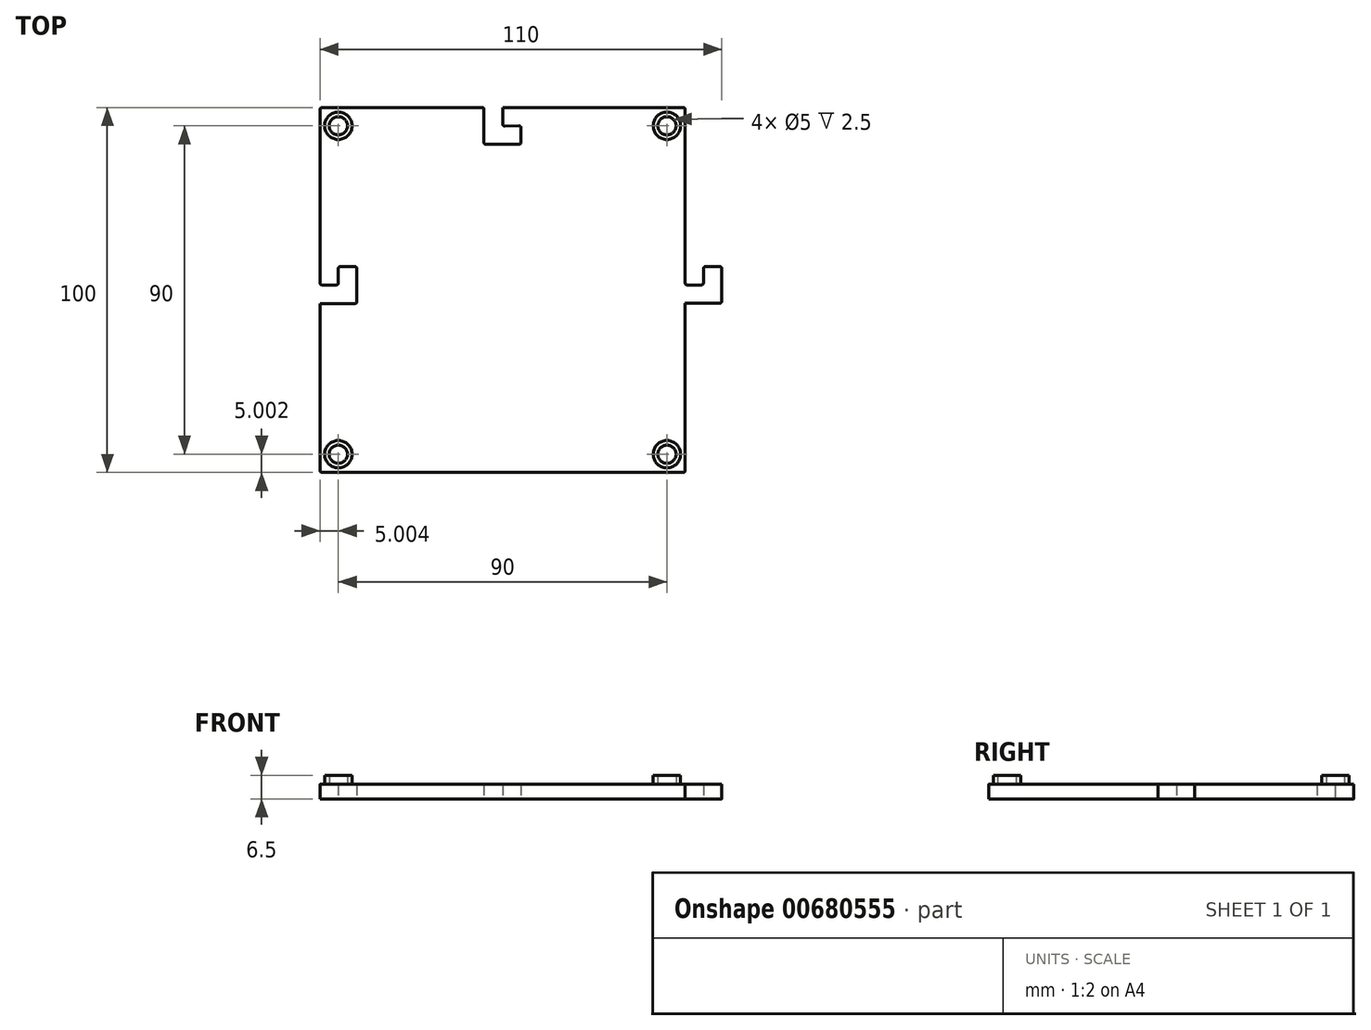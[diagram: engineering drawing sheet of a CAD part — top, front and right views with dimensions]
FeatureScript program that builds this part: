
annotation { "Feature Type Name" : "Feature", "Feature Type Description" : "" }
export const myFeature = defineFeature(function(context is Context, id is Id, definition is map)
    precondition{}
    {
        {
            var Q0;
            Q0=qCreatedBy(makeId("Top.planeOp"),FACE);
            var sketch = newSketch(context, id + "F0", { "sketchPlane" : qUnion([Q0])});
            skLineSegment(sketch, "E0.bottom", {"start": v(-68.75, 48.6) * mm, "end": v(31.25, 48.6) * mm});
            skLineSegment(sketch, "E0.top", {"start": v(-68.75, -51.4) * mm, "end": v(31.25, -51.4) * mm});
            skLineSegment(sketch, "E0.left", {"start": v(-68.75, 48.6) * mm, "end": v(-68.75, -51.4) * mm});
            skLineSegment(sketch, "E0.right", {"start": v(31.25, 48.6) * mm, "end": v(31.25, -51.4) * mm});
            skSolve(sketch);
        }
        {
            var Q0;
            Q0=makeQuery(id+"F0.imprint","IMPRINT",FACE,{"disambiguationData":[TD([[makeQuery(id+"F0.imprint","IMPRINT",EDGE,{"derivedFrom":sQuery(id+"F0.wireOp",EDGE,"E0.bottom")}),-1.0]])]});
            extrude(context, id + "F1", {"entities" : qUnion([Q0]), "depth" : 4 * mm, "offsetDistance" : 25 * mm});
        }
        {
            var Q0;
            Q0=makeQuery(id+"F1.opExtrude","CAP_FACE",FACE,{"disambiguationData":[OSD([sQuery(id+"F0.wireOp",EDGE,"E0.bottom"),sQuery(id+"F0.wireOp",EDGE,"E0.top"),sQuery(id+"F0.wireOp",EDGE,"E0.left"),sQuery(id+"F0.wireOp",EDGE,"E0.right")])],"isStart":true});
            var sketch = newSketch(context, id + "F2", { "sketchPlane" : qUnion([Q0])});
            skLineSegment(sketch, "E1.bottom", {"start": v(-18.75, 51.4) * mm, "end": v(-23.75, 51.4) * mm});
            skLineSegment(sketch, "E1.top", {"start": v(-18.75, 51.4) * mm, "end": v(-23.75, 51.4) * mm});
            skLineSegment(sketch, "E1.left", {"start": v(-18.75, 51.4) * mm, "end": v(-18.75, 51.4) * mm});
            skLineSegment(sketch, "E1.right", {"start": v(-23.75, 51.4) * mm, "end": v(-23.75, 51.4) * mm});
            skLineSegment(sketch, "E2", {"start": v(-18.75, 51.4) * mm, "end": v(-13.75, 51.4) * mm});
            skLineSegment(sketch, "E3", {"start": v(-23.75, 51.4) * mm, "end": v(-23.75, 61.4) * mm});
            skLineSegment(sketch, "E4", {"start": v(-23.75, 61.4) * mm, "end": v(-13.75, 61.4) * mm});
            skLineSegment(sketch, "E5", {"start": v(-13.75, 61.4) * mm, "end": v(-13.75, 51.4) * mm});
            skLineSegment(sketch, "E6", {"start": v(-18.75, 51.4) * mm, "end": v(-18.75, 56.4) * mm});
            skLineSegment(sketch, "E7", {"start": v(-18.75, 56.4) * mm, "end": v(-13.75, 56.4) * mm});
            skLineSegment(sketch, "E8", {"start": v(31.25, 0) * mm, "end": v(31.25, 5) * mm});
            skLineSegment(sketch, "E9", {"start": v(31.25, 0) * mm, "end": v(31.25, -5) * mm});
            skLineSegment(sketch, "E10", {"start": v(31.25, 5) * mm, "end": v(41.25, 5) * mm});
            skLineSegment(sketch, "E11", {"start": v(41.25, 5) * mm, "end": v(41.25, -5) * mm});
            skLineSegment(sketch, "E12", {"start": v(31.25, -5) * mm, "end": v(41.25, -5) * mm});
            skLineSegment(sketch, "E13", {"start": v(31.25, 0) * mm, "end": v(36.25, 0) * mm});
            skPoint(sketch, "E13.endSnap0", {"position": v(41.25, 0) * mm});
            skLineSegment(sketch, "E14", {"start": v(36.25, 0) * mm, "end": v(36.25, -5) * mm});
            skLineSegment(sketch, "E15", {"start": v(-18.75, -48.6) * mm, "end": v(-23.75, -48.6) * mm});
            skLineSegment(sketch, "E16", {"start": v(-18.75, -48.6) * mm, "end": v(-13.75, -48.6) * mm});
            skLineSegment(sketch, "E17", {"start": v(-23.75, -48.6) * mm, "end": v(-23.75, -38.6) * mm});
            skLineSegment(sketch, "E18", {"start": v(-23.75, -38.6) * mm, "end": v(-13.75, -38.6) * mm});
            skLineSegment(sketch, "E19", {"start": v(-13.75, -38.6) * mm, "end": v(-13.75, -48.6) * mm});
            skLineSegment(sketch, "E20", {"start": v(-18.75, -48.6) * mm, "end": v(-18.75, -43.6) * mm});
            skLineSegment(sketch, "E21", {"start": v(-18.75, -43.6) * mm, "end": v(-13.75, -43.6) * mm});
            skLineSegment(sketch, "E22", {"start": v(-68.75, 0) * mm, "end": v(-68.75, 5) * mm});
            skLineSegment(sketch, "E23", {"start": v(-68.75, 0) * mm, "end": v(-68.75, -5) * mm});
            skLineSegment(sketch, "E24", {"start": v(-68.75, 5) * mm, "end": v(-58.75, 5) * mm});
            skLineSegment(sketch, "E25", {"start": v(-58.75, 5) * mm, "end": v(-58.75, -5) * mm});
            skLineSegment(sketch, "E26", {"start": v(-68.75, -5) * mm, "end": v(-58.75, -5) * mm});
            skLineSegment(sketch, "E27", {"start": v(-68.75, 0) * mm, "end": v(-63.75, 0) * mm});
            skLineSegment(sketch, "E28", {"start": v(-63.75, 0) * mm, "end": v(-63.75, -5) * mm});
            skSolve(sketch);
        }
        {
            var Q0;
            Q0=makeQuery(id+"F2.imprint","IMPRINT",FACE,{"disambiguationData":[TD([[makeQuery(id+"F2.imprint","IMPRINT",EDGE,{"derivedFrom":sQuery(id+"F2.wireOp",EDGE,"E1.top")}),1.0]])]});
            var Q1;
            Q1=makeQuery(id+"F2.imprint","IMPRINT",FACE,{"disambiguationData":[TD([[makeQuery(id+"F2.imprint","IMPRINT",EDGE,{"derivedFrom":sQuery(id+"F2.wireOp",EDGE,"E8")}),-1.0]])]});
            extrude(context, id + "F3", {"entities" : qUnion([Q0, Q1]), "oppositeDirection" : true, "depth" : 4 * mm, "offsetDistance" : 25 * mm});
        }
        {
            var Q0;
            Q0=makeQuery(id+"F1.opExtrude","CAP_FACE",FACE,{"disambiguationData":[OSD([sQuery(id+"F0.wireOp",EDGE,"E0.bottom"),sQuery(id+"F0.wireOp",EDGE,"E0.top"),sQuery(id+"F0.wireOp",EDGE,"E0.left"),sQuery(id+"F0.wireOp",EDGE,"E0.right")])],"isStart":true});
            var sketch = newSketch(context, id + "F4", { "sketchPlane" : qUnion([Q0])});
            skLineSegment(sketch, "E29", {"start": v(-18.75, -48.6) * mm, "end": v(-23.85, -48.6) * mm});
            skLineSegment(sketch, "E30", {"start": v(-23.85, -48.6) * mm, "end": v(-23.85, -38.5) * mm});
            skLineSegment(sketch, "E31", {"start": v(-18.75, -48.6) * mm, "end": v(-18.75, -43.55) * mm});
            skPoint(sketch, "E31.endSnap0", {"position": v(-23.85, -43.55) * mm});
            skLineSegment(sketch, "E32", {"start": v(-18.75, -43.55) * mm, "end": v(-13.75, -43.6) * mm});
            skLineSegment(sketch, "E33", {"start": v(-68.75, 0) * mm, "end": v(-68.75, 5.1) * mm});
            skLineSegment(sketch, "E34", {"start": v(-68.75, 5.1) * mm, "end": v(-58.65, 5.1) * mm});
            skLineSegment(sketch, "E35", {"start": v(-68.75, 0) * mm, "end": v(-63.75, 0) * mm});
            skLineSegment(sketch, "E36", {"start": v(-63.75, 0) * mm, "end": v(-63.75, -5) * mm});
            skLineSegment(sketch, "E37", {"start": v(-63.75, -5) * mm, "end": v(-58.65, -5) * mm});
            skLineSegment(sketch, "E38", {"start": v(-58.65, 5.1) * mm, "end": v(-58.65, -5) * mm});
            skLineSegment(sketch, "E39", {"start": v(-13.75, -43.6) * mm, "end": v(-13.75, -38.5) * mm});
            skLineSegment(sketch, "E40", {"start": v(-23.85, -38.5) * mm, "end": v(-13.75, -38.5) * mm});
            skSolve(sketch);
        }
        {
            var Q0;
            Q0 = qSketchRegion(id + "F4", true);
            extrude(context, id + "F5", {"entities" : qUnion([Q0]), "operationType" : NewBodyOperationType.REMOVE, "oppositeDirection" : true, "depth" : 25 * mm, "offsetDistance" : 25 * mm});
        }
        {
            var Q0;
            Q0=makeQuery(id+"F1.opExtrude","SWEPT_EDGE",EDGE,{"disambiguationData":[OSD([sQuery(id+"F0.wireOp",EDGE,"E0.top"),sQuery(id+"F0.wireOp",EDGE,"E0.right")])]});
            var Q1;
            Q1=makeQuery(id+"F1.opExtrude","SWEPT_EDGE",EDGE,{"disambiguationData":[OSD([sQuery(id+"F0.wireOp",EDGE,"E0.bottom"),sQuery(id+"F0.wireOp",EDGE,"E0.right")])]});
            var Q2;
            Q2=makeQuery(id+"F1.opExtrude","SWEPT_EDGE",EDGE,{"disambiguationData":[OSD([sQuery(id+"F0.wireOp",EDGE,"E0.bottom"),sQuery(id+"F0.wireOp",EDGE,"E0.left")])]});
            var Q3;
            Q3=makeQuery(id+"F1.opExtrude","SWEPT_EDGE",EDGE,{"disambiguationData":[OSD([sQuery(id+"F0.wireOp",EDGE,"E0.top"),sQuery(id+"F0.wireOp",EDGE,"E0.left")])]});
            fillet(context, id + "F6", {"entities" : qUnion([Q0, Q1, Q2, Q3]), "radius" : 0.5 * mm, "tangentPropagation" : true, "allowEdgeOverflow" : false});
        }
        {
            var Q0;
            Q0=makeQuery(id+"F3.opExtrude","SWEPT_BODY",BODY,{"disambiguationData":[OSD([sQuery(id+"F2.wireOp",EDGE,"E1.top"),sQuery(id+"F2.wireOp",EDGE,"E3"),sQuery(id+"F2.wireOp",EDGE,"E4"),sQuery(id+"F2.wireOp",EDGE,"E5"),sQuery(id+"F2.wireOp",EDGE,"E6"),sQuery(id+"F2.wireOp",EDGE,"E7")])]});
            var Q1;
            Q1=makeQuery(id+"F1.opExtrude","SWEPT_BODY",BODY,{"disambiguationData":[OSD([sQuery(id+"F0.wireOp",EDGE,"E0.bottom"),sQuery(id+"F0.wireOp",EDGE,"E0.top"),sQuery(id+"F0.wireOp",EDGE,"E0.left"),sQuery(id+"F0.wireOp",EDGE,"E0.right")])]});
            var Q2;
            Q2=makeQuery(id+"F3.opExtrude","SWEPT_BODY",BODY,{"disambiguationData":[OSD([sQuery(id+"F2.wireOp",EDGE,"E8"),sQuery(id+"F2.wireOp",EDGE,"E10"),sQuery(id+"F2.wireOp",EDGE,"E11"),sQuery(id+"F2.wireOp",EDGE,"E12"),sQuery(id+"F2.wireOp",EDGE,"E13"),sQuery(id+"F2.wireOp",EDGE,"E14")])]});
            booleanBodies(context, id + "F7", {"operationType" : BooleanOperationType.UNION, "tools" : qUnion([Q0, Q1, Q2])});
        }
        {
            var Q0;
            Q0=makeQuery(id+"F3.opExtrude","SWEPT_EDGE",EDGE,{"disambiguationData":[OSD([sQuery(id+"F0.wireOp",EDGE,"E0.top"),sQuery(id+"F2.wireOp",EDGE,"E1.top"),sQuery(id+"F2.wireOp",EDGE,"E3")])]});
            var Q1;
            Q1=makeQuery(id+"F3.opExtrude","SWEPT_EDGE",EDGE,{"disambiguationData":[OSD([sQuery(id+"F2.wireOp",EDGE,"E1.top"),sQuery(id+"F2.wireOp",EDGE,"E2"),sQuery(id+"F2.wireOp",EDGE,"E6")])]});
            var Q2;
            Q2=makeQuery(id+"F3.opExtrude","SWEPT_EDGE",EDGE,{"disambiguationData":[OSD([sQuery(id+"F2.wireOp",EDGE,"E4"),sQuery(id+"F2.wireOp",EDGE,"E5")])]});
            var Q3;
            Q3=makeQuery(id+"F3.opExtrude","SWEPT_EDGE",EDGE,{"disambiguationData":[OSD([sQuery(id+"F2.wireOp",EDGE,"E5"),sQuery(id+"F2.wireOp",EDGE,"E7")])]});
            var Q4;
            Q4=makeQuery(id+"F3.opExtrude","SWEPT_EDGE",EDGE,{"disambiguationData":[OSD([sQuery(id+"F2.wireOp",EDGE,"E6"),sQuery(id+"F2.wireOp",EDGE,"E7")])]});
            var Q5;
            Q5=makeQuery(id+"F3.opExtrude","SWEPT_EDGE",EDGE,{"disambiguationData":[OSD([sQuery(id+"F2.wireOp",EDGE,"E3"),sQuery(id+"F2.wireOp",EDGE,"E4")])]});
            var Q6;
            Q6=makeQuery(id+"F3.opExtrude","SWEPT_EDGE",EDGE,{"disambiguationData":[OSD([sQuery(id+"F0.wireOp",EDGE,"E0.right"),sQuery(id+"F2.wireOp",EDGE,"E8"),sQuery(id+"F2.wireOp",EDGE,"E10")])]});
            var Q7;
            Q7=makeQuery(id+"F3.opExtrude","SWEPT_EDGE",EDGE,{"disambiguationData":[OSD([sQuery(id+"F2.wireOp",EDGE,"E10"),sQuery(id+"F2.wireOp",EDGE,"E11")])]});
            var Q8;
            Q8=makeQuery(id+"F3.opExtrude","SWEPT_EDGE",EDGE,{"disambiguationData":[OSD([sQuery(id+"F2.wireOp",EDGE,"E11"),sQuery(id+"F2.wireOp",EDGE,"E12")])]});
            var Q9;
            Q9=makeQuery(id+"F3.opExtrude","SWEPT_EDGE",EDGE,{"disambiguationData":[OSD([sQuery(id+"F2.wireOp",EDGE,"E12"),sQuery(id+"F2.wireOp",EDGE,"E14")])]});
            var Q10;
            Q10=makeQuery(id+"F3.opExtrude","SWEPT_EDGE",EDGE,{"disambiguationData":[OSD([sQuery(id+"F2.wireOp",EDGE,"E13"),sQuery(id+"F2.wireOp",EDGE,"E14")])]});
            var Q11;
            Q11=makeQuery(id+"F3.opExtrude","SWEPT_EDGE",EDGE,{"disambiguationData":[OSD([sQuery(id+"F2.wireOp",EDGE,"E8"),sQuery(id+"F2.wireOp",EDGE,"E9"),sQuery(id+"F2.wireOp",EDGE,"E13")])]});
            var Q12;
            Q12=makeQuery(id+"F5.boolean.opBoolean","COPY",EDGE,{"derivedFrom":makeQuery(id+"F5.opExtrude","SWEPT_EDGE",EDGE,{"disambiguationData":[OSD([sQuery(id+"F4.wireOp",EDGE,"E30"),sQuery(id+"F4.wireOp",EDGE,"E40")])]})});
            var Q13;
            Q13=makeQuery(id+"F5.boolean.opBoolean","COPY",EDGE,{"derivedFrom":makeQuery(id+"F5.opExtrude","SWEPT_EDGE",EDGE,{"disambiguationData":[OSD([sQuery(id+"F4.wireOp",EDGE,"E39"),sQuery(id+"F4.wireOp",EDGE,"E40")])]})});
            var Q14;
            Q14=makeQuery(id+"F5.boolean.opBoolean","COPY",EDGE,{"derivedFrom":makeQuery(id+"F5.opExtrude","SWEPT_EDGE",EDGE,{"disambiguationData":[OSD([sQuery(id+"F0.wireOp",EDGE,"E0.bottom"),sQuery(id+"F4.wireOp",EDGE,"E29"),sQuery(id+"F4.wireOp",EDGE,"E31")])]})});
            var Q15;
            Q15=makeQuery(id+"F5.boolean.opBoolean","COPY",EDGE,{"derivedFrom":makeQuery(id+"F5.opExtrude","SWEPT_EDGE",EDGE,{"disambiguationData":[OSD([sQuery(id+"F4.wireOp",EDGE,"E31"),sQuery(id+"F4.wireOp",EDGE,"E32")])]})});
            var Q16;
            Q16=makeQuery(id+"F5.boolean.opBoolean","COPY",EDGE,{"derivedFrom":makeQuery(id+"F5.opExtrude","SWEPT_EDGE",EDGE,{"disambiguationData":[OSD([sQuery(id+"F0.wireOp",EDGE,"E0.bottom"),sQuery(id+"F4.wireOp",EDGE,"E29"),sQuery(id+"F4.wireOp",EDGE,"E30")])]})});
            var Q17;
            Q17=makeQuery(id+"F5.boolean.opBoolean","COPY",EDGE,{"derivedFrom":makeQuery(id+"F5.opExtrude","SWEPT_EDGE",EDGE,{"disambiguationData":[OSD([sQuery(id+"F4.wireOp",EDGE,"E32"),sQuery(id+"F4.wireOp",EDGE,"E39")])]})});
            fillet(context, id + "F8", {"entities" : qUnion([Q0, Q1, Q2, Q3, Q4, Q5, Q6, Q7, Q8, Q9, Q10, Q11, Q12, Q13, Q14, Q15, Q16, Q17]), "radius" : 0.5 * mm, "tangentPropagation" : true, "allowEdgeOverflow" : false});
        }
        {
            var Q0;
            Q0=makeQuery(id+"F5.boolean.opBoolean","COPY",EDGE,{"derivedFrom":makeQuery(id+"F5.opExtrude","SWEPT_EDGE",EDGE,{"disambiguationData":[OSD([sQuery(id+"F4.wireOp",EDGE,"E37"),sQuery(id+"F4.wireOp",EDGE,"E38")])]})});
            var Q1;
            Q1=makeQuery(id+"F5.boolean.opBoolean","COPY",EDGE,{"derivedFrom":makeQuery(id+"F5.opExtrude","SWEPT_EDGE",EDGE,{"disambiguationData":[OSD([sQuery(id+"F0.wireOp",EDGE,"E0.left"),sQuery(id+"F4.wireOp",EDGE,"E33"),sQuery(id+"F4.wireOp",EDGE,"E35")])]})});
            fillet(context, id + "F9", {"entities" : qUnion([Q0, Q1]), "radius" : 0.5 * mm, "tangentPropagation" : true, "allowEdgeOverflow" : false});
        }
        {
            var Q0;
            Q0=makeQuery(id+"F5.boolean.opBoolean","COPY",EDGE,{"derivedFrom":makeQuery(id+"F5.opExtrude","SWEPT_EDGE",EDGE,{"disambiguationData":[OSD([sQuery(id+"F4.wireOp",EDGE,"E35"),sQuery(id+"F4.wireOp",EDGE,"E36")])]})});
            var Q1;
            Q1=makeQuery(id+"F5.boolean.opBoolean","COPY",EDGE,{"derivedFrom":makeQuery(id+"F5.opExtrude","SWEPT_EDGE",EDGE,{"disambiguationData":[OSD([sQuery(id+"F4.wireOp",EDGE,"E36"),sQuery(id+"F4.wireOp",EDGE,"E37")])]})});
            var Q2;
            Q2=makeQuery(id+"F5.boolean.opBoolean","COPY",EDGE,{"derivedFrom":makeQuery(id+"F5.opExtrude","SWEPT_EDGE",EDGE,{"disambiguationData":[OSD([sQuery(id+"F4.wireOp",EDGE,"E34"),sQuery(id+"F4.wireOp",EDGE,"E38")])]})});
            var Q3;
            Q3=makeQuery(id+"F5.boolean.opBoolean","COPY",EDGE,{"derivedFrom":makeQuery(id+"F5.opExtrude","SWEPT_EDGE",EDGE,{"disambiguationData":[OSD([sQuery(id+"F0.wireOp",EDGE,"E0.left"),sQuery(id+"F4.wireOp",EDGE,"E33"),sQuery(id+"F4.wireOp",EDGE,"E34")])]})});
            fillet(context, id + "F10", {"entities" : qUnion([Q0, Q1, Q2, Q3]), "radius" : 0.5 * mm, "tangentPropagation" : true, "allowEdgeOverflow" : false});
        }
        {
            var Q0;
            Q0=makeQuery(id+"F7.opBoolean","MERGE",FACE,{"derivedFrom":[makeQuery(id+"F3.opExtrude","CAP_FACE",FACE,{"disambiguationData":[OSD([sQuery(id+"F2.wireOp",EDGE,"E1.top"),sQuery(id+"F2.wireOp",EDGE,"E3"),sQuery(id+"F2.wireOp",EDGE,"E4"),sQuery(id+"F2.wireOp",EDGE,"E5"),sQuery(id+"F2.wireOp",EDGE,"E6"),sQuery(id+"F2.wireOp",EDGE,"E7")])],"isStart":false}),makeQuery(id+"F3.opExtrude","CAP_FACE",FACE,{"disambiguationData":[OSD([sQuery(id+"F2.wireOp",EDGE,"E8"),sQuery(id+"F2.wireOp",EDGE,"E10"),sQuery(id+"F2.wireOp",EDGE,"E11"),sQuery(id+"F2.wireOp",EDGE,"E12"),sQuery(id+"F2.wireOp",EDGE,"E13"),sQuery(id+"F2.wireOp",EDGE,"E14")])],"isStart":false}),makeQuery(id+"F1.opExtrude","CAP_FACE",FACE,{"disambiguationData":[OSD([sQuery(id+"F0.wireOp",EDGE,"E0.bottom"),sQuery(id+"F0.wireOp",EDGE,"E0.top"),sQuery(id+"F0.wireOp",EDGE,"E0.left"),sQuery(id+"F0.wireOp",EDGE,"E0.right")])],"isStart":false})]});
            var sketch = newSketch(context, id + "F11", { "sketchPlane" : qUnion([Q0])});
            skCircle(sketch, "E41", {"center": v(-63.75, 43.6) * mm, "radius": 3.75 * mm});
            skCircle(sketch, "E42", {"center": v(26.25, 43.6) * mm, "radius": 3.75 * mm});
            skCircle(sketch, "E43", {"center": v(26.25, -46.4) * mm, "radius": 3.75 * mm});
            skCircle(sketch, "E44", {"center": v(-63.75, -46.4) * mm, "radius": 3.75 * mm});
            skCircle(sketch, "E45", {"center": v(-63.75, 43.6) * mm, "radius": 2.5 * mm});
            skCircle(sketch, "E46", {"center": v(26.25, 43.6) * mm, "radius": 2.5 * mm});
            skCircle(sketch, "E47", {"center": v(-63.75, -46.4) * mm, "radius": 2.5 * mm});
            skCircle(sketch, "E48", {"center": v(26.25, -46.4) * mm, "radius": 2.5 * mm});
            skSolve(sketch);
        }
        {
            var Q0;
            Q0=makeQuery(id+"F11.imprint","IMPRINT",FACE,{"disambiguationData":[TD([[makeQuery(id+"F11.imprint","IMPRINT",EDGE,{"derivedFrom":sQuery(id+"F11.wireOp",EDGE,"E41")}),1.0]])]});
            var Q1;
            Q1=makeQuery(id+"F11.imprint","IMPRINT",FACE,{"disambiguationData":[TD([[makeQuery(id+"F11.imprint","IMPRINT",EDGE,{"derivedFrom":sQuery(id+"F11.wireOp",EDGE,"E42")}),1.0]])]});
            var Q2;
            Q2=makeQuery(id+"F11.imprint","IMPRINT",FACE,{"disambiguationData":[TD([[makeQuery(id+"F11.imprint","IMPRINT",EDGE,{"derivedFrom":sQuery(id+"F11.wireOp",EDGE,"E43")}),1.0]])]});
            var Q3;
            Q3=makeQuery(id+"F11.imprint","IMPRINT",FACE,{"disambiguationData":[TD([[makeQuery(id+"F11.imprint","IMPRINT",EDGE,{"derivedFrom":sQuery(id+"F11.wireOp",EDGE,"E44")}),1.0]])]});
            extrude(context, id + "F12", {"entities" : qUnion([Q0, Q1, Q2, Q3]), "operationType" : NewBodyOperationType.ADD, "depth" : 2.5 * mm, "offsetDistance" : 25 * mm});
        }
    });
